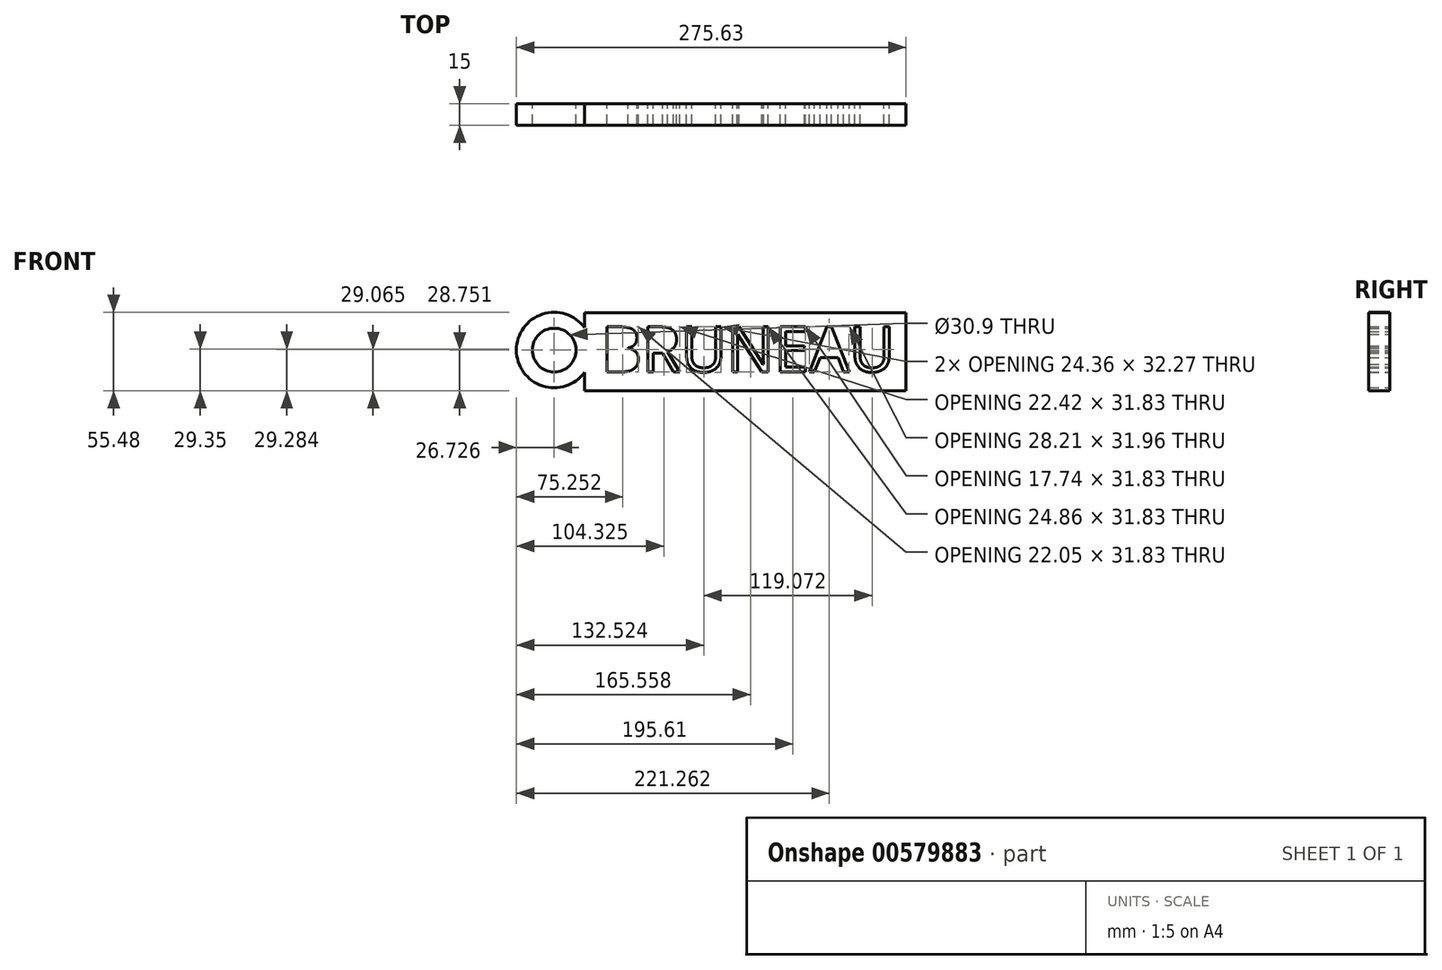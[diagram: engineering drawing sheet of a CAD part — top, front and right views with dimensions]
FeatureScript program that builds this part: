
annotation { "Feature Type Name" : "Feature", "Feature Type Description" : "" }
export const myFeature = defineFeature(function(context is Context, id is Id, definition is map)
    precondition{}
    {
        {
            var Q0;
            Q0=qCreatedBy(makeId("Front.planeOp"),FACE);
            var sketch = newSketch(context, id + "F0", { "sketchPlane" : qUnion([Q0])});
            skLineSegment(sketch, "E0.bottom", {"start": v(-74, 25.86) * mm, "end": v(153.36, 25.86) * mm});
            skLineSegment(sketch, "E0.top", {"start": v(-74, -29.42) * mm, "end": v(153.36, -29.42) * mm});
            skLineSegment(sketch, "E0.left", {"start": v(-74, 25.86) * mm, "end": v(-74, 15.16) * mm});
            skLineSegment(sketch, "E0.right", {"start": v(153.36, 25.86) * mm, "end": v(153.36, -29.42) * mm});
            skArc(sketch, "E1", {"start": v(-74, 15.16) * mm, "mid": v(-122.27, -0.67) * mm, "end": v(-74, -16.5) * mm});
            skCircle(sketch, "E2", {"center": v(-95.54, -0.67) * mm, "radius": 15.45 * mm});
            skText(sketch, "E3", { "text": "BRUNEAU", "fontName": "OpenSans-Regular.ttf"});
            skLineSegment(sketch, "E4.trimOffspring", {"start": v(-74, -16.5) * mm, "end": v(-74, -29.42) * mm});
            const initialGuessF0  = {"E3": [-0.06242, -0.01605, 1, 0, 0.0321]};
            skSetInitialGuess(sketch, initialGuessF0);
            skSolve(sketch);
        }
        {
            var Q0;
            Q0 = qSketchRegion(id + "F0", true);
            extrude(context, id + "F1", {"entities" : qUnion([Q0]), "depth" : 15 * mm, "offsetDistance" : 25 * mm});
        }
    });
